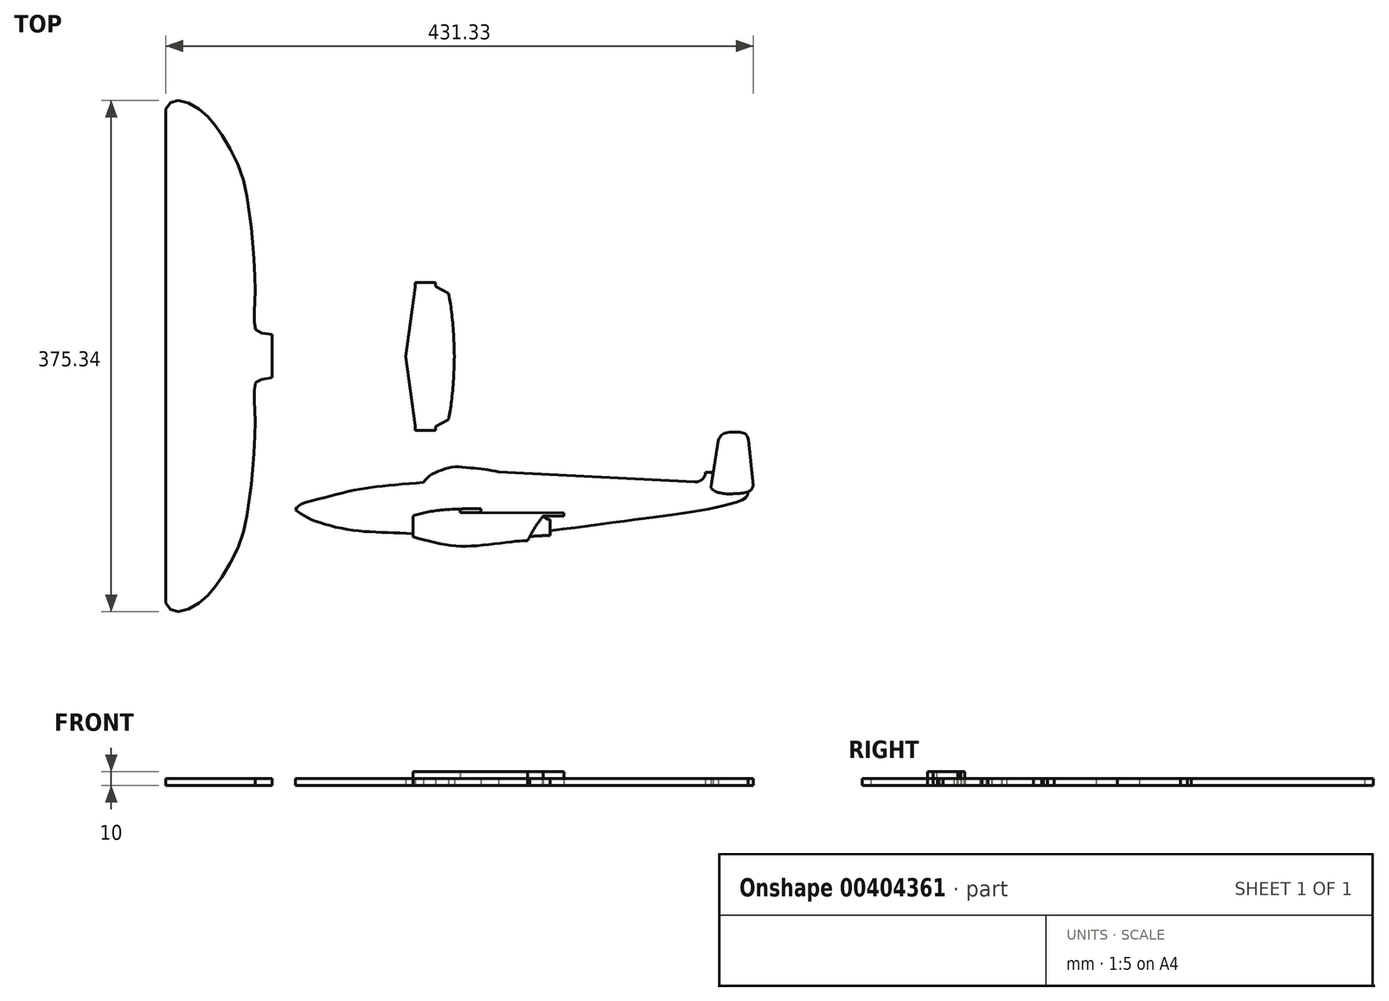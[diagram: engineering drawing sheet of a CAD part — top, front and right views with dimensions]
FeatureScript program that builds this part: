
annotation { "Feature Type Name" : "Feature", "Feature Type Description" : "" }
export const myFeature = defineFeature(function(context is Context, id is Id, definition is map)
    precondition{}
    {
        {
            var Q0;
            Q0=qCreatedBy(makeId("Top.planeOp"),FACE);
            var sketch = newSketch(context, id + "F0", { "sketchPlane" : qUnion([Q0])});
            skLineSegment(sketch, "E0", {"start": v(-207.66, -171.28) * mm, "end": v(-207.66, 10) * mm});
            skFitSpline(sketch, "E1", {"points": [v(-207.66, 10) * mm, v(-202.85, 15.7) * mm, v(-191.9, 14.82) * mm, v(-178.34, 6.06) * mm, v(-168.71, -5.75) * mm, v(-153.4, -33.76) * mm, v(-146.4, -65.7) * mm, v(-143.33, -93.72) * mm, v(-142.01, -124.35) * mm, v(-142.45, -136.6) * mm, v(-142.45, -149.3) * mm, v(-140.26, -153.23) * mm, v(-129.76, -155.42) * mm], "startDerivative": vector(68.67, 123.88) * mm, "endDerivative": vector(186.35, -20.01) * mm});
            skLineSegment(sketch, "E2", {"start": v(-129.76, -155.42) * mm, "end": v(-129.76, -171.28) * mm});
            skLineSegment(sketch, "E3.MirrorCS", {"start": v(-207.66, -171.28) * mm, "end": v(-207.66, -352.57) * mm});
            skLineSegment(sketch, "E4.MirrorCS", {"start": v(-129.76, -187.14) * mm, "end": v(-129.76, -171.28) * mm});
            skFitSpline(sketch, "E5.MirrorCS", {"points": [v(-207.66, -352.57) * mm, v(-202.85, -358.25) * mm, v(-191.9, -357.38) * mm, v(-178.34, -348.63) * mm, v(-168.71, -336.81) * mm, v(-153.4, -308.8) * mm, v(-146.4, -276.86) * mm, v(-143.33, -248.85) * mm, v(-142.01, -218.21) * mm, v(-142.45, -205.96) * mm, v(-142.45, -193.27) * mm, v(-140.26, -189.33) * mm, v(-129.76, -187.14) * mm], "startDerivative": vector(68.67, -123.88) * mm, "endDerivative": vector(186.35, 20.01) * mm});
            skFitSpline(sketch, "E6", {"points": [v(-112.4, -284.3) * mm, v(-109.82, -280.98) * mm, v(-92.52, -275.46) * mm, v(-68.6, -269.57) * mm, v(-48, -266.63) * mm, v(-18.55, -264.05) * mm], "startDerivative": vector(17.03, 35.63) * mm, "endDerivative": vector(121.12, 9.89) * mm});
            skFitSpline(sketch, "E7", {"points": [v(-18.55, -264.05) * mm, v(-13.4, -258.9) * mm, v(-4.94, -254.85) * mm, v(4.26, -252.65) * mm, v(16.4, -253.38) * mm, v(26.71, -254.49) * mm, v(36.65, -256.33) * mm], "startDerivative": vector(31.81, 38.04) * mm, "endDerivative": vector(58.7, -12.14) * mm});
            skLineSegment(sketch, "E8", {"start": v(36.65, -256.33) * mm, "end": v(180.9, -263.69) * mm});
            skArc(sketch, "E9", {"start": v(180.9, -263.69) * mm, "mid": v(186.22, -261.8) * mm, "end": v(188.63, -256.7) * mm});
            skLineSegment(sketch, "E10", {"start": v(188.63, -256.7) * mm, "end": v(215.5, -256.7) * mm});
            skFitSpline(sketch, "E11", {"points": [v(215.5, -256.7) * mm, v(219.18, -265.53) * mm, v(219.91, -271.05) * mm, v(218.44, -275.1) * mm, v(206.67, -279.88) * mm, v(183.11, -285.03) * mm, v(148.52, -289.81) * mm, v(90.38, -297.54) * mm, v(23.4, -303.06) * mm, v(-35.11, -301.22) * mm, v(-70.8, -299.01) * mm, v(-100.62, -291.29) * mm, v(-112.4, -284.3) * mm], "startDerivative": vector(85.33, -181.2) * mm, "endDerivative": vector(-165, 117.6) * mm});
            skLineSegment(sketch, "E12", {"start": v(-25.95, -288.57) * mm, "end": v(-25.95, -304.06) * mm});
            skLineSegment(sketch, "E13", {"start": v(74.67, -291.4) * mm, "end": v(74.67, -302.86) * mm});
            skFitSpline(sketch, "E14", {"points": [v(23.76, -283.27) * mm, v(0, -283.88) * mm, v(-15.1, -285.68) * mm, v(-25.95, -288.57) * mm], "startDerivative": vector(-62.09, -0.7) * mm, "endDerivative": vector(-37.97, -11.96) * mm});
            skFitSpline(sketch, "E15", {"points": [v(-25.95, -304.06) * mm, v(0, -310.09) * mm, v(25.57, -310.09) * mm, v(51.17, -307.07) * mm, v(58.1, -306.77) * mm], "startDerivative": vector(91.04, -25.6) * mm, "endDerivative": vector(39.1, 0.17) * mm});
            skFitSpline(sketch, "E16", {"points": [v(58.1, -306.77) * mm, v(63.23, -297.43) * mm, v(69.55, -288.57) * mm], "startDerivative": vector(9.7, 19.07) * mm, "endDerivative": vector(13.2, 17.09) * mm});
            skLineSegment(sketch, "E17", {"start": v(69.55, -288.57) * mm, "end": v(84.69, -288.57) * mm});
            skLineSegment(sketch, "E18", {"start": v(23.76, -286.24) * mm, "end": v(23.76, -283.27) * mm});
            skFitSpline(sketch, "E19", {"points": [v(59.71, -303.61) * mm, v(74.67, -302.86) * mm], "startDerivative": vector(15.26, 0.75) * mm, "endDerivative": vector(15.26, 0.75) * mm});
            skLineSegment(sketch, "E20", {"start": v(84.69, -288.57) * mm, "end": v(84.69, -286.35) * mm});
            skLineSegment(sketch, "E21", {"start": v(23.76, -286.24) * mm, "end": v(84.69, -286.35) * mm});
            skLineSegment(sketch, "E22", {"start": v(8.37, -283.52) * mm, "end": v(8.37, -286.28) * mm});
            skLineSegment(sketch, "E23", {"start": v(23.76, -286.24) * mm, "end": v(8.37, -286.28) * mm});
            skFitSpline(sketch, "E24", {"points": [v(59.9, -286.3) * mm, v(66.14, -288.1) * mm, v(70.51, -289.69) * mm, v(71.8, -290.67) * mm, v(74.67, -291.4) * mm], "startDerivative": vector(18.97, -5.44) * mm, "endDerivative": vector(14.81, -2.5) * mm});
            skLineSegment(sketch, "E25", {"start": v(-24.57, -117.33) * mm, "end": v(-24.57, -120.63) * mm});
            skLineSegment(sketch, "E26", {"start": v(-24.57, -120.63) * mm, "end": v(-31.45, -171.53) * mm});
            skLineSegment(sketch, "E27", {"start": v(-24.57, -117.33) * mm, "end": v(-9.72, -117.33) * mm});
            skLineSegment(sketch, "E28", {"start": v(-9.72, -117.33) * mm, "end": v(-9.72, -120.08) * mm});
            skLineSegment(sketch, "E29", {"start": v(-9.72, -120.08) * mm, "end": v(0, -125.3) * mm});
            skFitSpline(sketch, "E30", {"points": [v(0, -125.3) * mm, v(2.66, -142.92) * mm, v(4.31, -171.53) * mm], "startDerivative": vector(6.72, -37.47) * mm, "endDerivative": vector(2.09, -54.3) * mm});
            skFitSpline(sketch, "E31.MirrorCS", {"points": [v(0, -217.75) * mm, v(2.66, -200.15) * mm, v(4.31, -171.53) * mm], "startDerivative": vector(6.72, 37.47) * mm, "endDerivative": vector(2.09, 54.3) * mm});
            skLineSegment(sketch, "E32.MirrorCS", {"start": v(-24.57, -225.73) * mm, "end": v(-9.72, -225.73) * mm});
            skLineSegment(sketch, "E33.MirrorCS", {"start": v(-9.72, -225.73) * mm, "end": v(-9.72, -222.98) * mm});
            skLineSegment(sketch, "E34.MirrorCS", {"start": v(-9.72, -222.98) * mm, "end": v(0, -217.75) * mm});
            skLineSegment(sketch, "E35.MirrorCS", {"start": v(-24.57, -225.73) * mm, "end": v(-24.57, -222.43) * mm});
            skLineSegment(sketch, "E36.MirrorCS", {"start": v(-24.57, -222.43) * mm, "end": v(-31.45, -171.53) * mm});
            skFitSpline(sketch, "E37", {"points": [v(197.94, -233.24) * mm, v(199.6, -230.08) * mm, v(202.48, -228.01) * mm, v(207.57, -227.05) * mm, v(212.25, -227.05) * mm, v(215.83, -227.46) * mm, v(219, -229.53) * mm, v(220.23, -233.24) * mm], "startDerivative": vector(10.44, 25.16) * mm, "endDerivative": vector(5.19, -28.6) * mm});
            skLineSegment(sketch, "E38", {"start": v(220.23, -233.24) * mm, "end": v(223.67, -266.4) * mm});
            skLineSegment(sketch, "E39", {"start": v(197.94, -233.24) * mm, "end": v(192.58, -267.9) * mm});
            skFitSpline(sketch, "E40", {"points": [v(192.58, -267.9) * mm, v(195.33, -270.38) * mm, v(200.14, -271.9) * mm, v(205.65, -272.45) * mm, v(212.11, -272.17) * mm, v(217.9, -271.62) * mm, v(222.15, -269.42) * mm, v(223.67, -266.4) * mm], "startDerivative": vector(19.57, -21.97) * mm, "endDerivative": vector(8.87, 27.2) * mm});
            skSolve(sketch);
        }
        {
            var Q0;
            Q0=makeQuery(id+"F0.imprint","IMPRINT",FACE,{"disambiguationData":[TD([[makeQuery(id+"F0.imprint","IMPRINT",EDGE,{"derivedFrom":sQuery(id+"F0.wireOp",EDGE,"E0")}),-1.0]])]});
            extrude(context, id + "F1", {"entities" : qUnion([Q0]), "depth" : 5 * mm});
        }
        {
            var Q0;
            Q0=makeQuery(id+"F0.imprint","IMPRINT",FACE,{"disambiguationData":[TD([[makeQuery(id+"F0.imprint","IMPRINT",EDGE,{"derivedFrom":sQuery(id+"F0.wireOp",EDGE,"E6")}),-1.0]])]});
            extrude(context, id + "F2", {"entities" : qUnion([Q0]), "depth" : 5 * mm});
        }
        {
            var Q0;
            {var subQ9=sQuery(id+"F0.wireOp",EDGE,"E22");Q0=makeQuery(id+"F0.imprint","IMPRINT",FACE,{"disambiguationData":[TD([[makeQuery(id+"F0.imprint","IMPRINT",EDGE,{"derivedFrom":subQ9}),-1.0]])]});}
            var Q1;
            {var subQ1=sQuery(id+"F0.wireOp",EDGE,"E15");Q1=makeQuery(id+"F0.imprint","IMPRINT",FACE,{"disambiguationData":[TD([[makeQuery(id+"F0.imprint","IMPRINT",EDGE,{"derivedFrom":subQ1}),1.0]])]});}
            var Q2;
            {var subQ0=sQuery(id+"F0.wireOp",EDGE,"E18");Q2=makeQuery(id+"F0.imprint","IMPRINT",FACE,{"disambiguationData":[TD([[makeQuery(id+"F0.imprint","IMPRINT",EDGE,{"derivedFrom":subQ0}),1.0]])]});}
            var Q3;
            {var subQ4=sQuery(id+"F0.wireOp",EDGE,"E17");Q3=makeQuery(id+"F0.imprint","IMPRINT",FACE,{"disambiguationData":[TD([[makeQuery(id+"F0.imprint","IMPRINT",EDGE,{"derivedFrom":subQ4}),1.0]])]});}
            var Q4;
            {var subQ0=sQuery(id+"F0.wireOp",EDGE,"E13");var subQ1=sQuery(id+"F0.wireOp",EDGE,"E11");var subQ2=makeQuery(id+"F0.imprint","INTERSECT",VERTEX,{"derivedFrom":[subQ1,subQ0]});Q4=makeQuery(id+"F0.imprint","IMPRINT",FACE,{"disambiguationData":[TD([[makeQuery(id+"F0.imprint","IMPRINT",EDGE,{"disambiguationData":[TD([[subQ2,-1.0]])],"derivedFrom":subQ1}),-1.0]])]});}
            var Q5;
            {var subQ0=sQuery(id+"F0.wireOp",EDGE,"E13");var subQ1=sQuery(id+"F0.wireOp",EDGE,"E11");var subQ2=makeQuery(id+"F0.imprint","INTERSECT",VERTEX,{"derivedFrom":[subQ1,subQ0]});Q5=makeQuery(id+"F0.imprint","IMPRINT",FACE,{"disambiguationData":[TD([[makeQuery(id+"F0.imprint","IMPRINT",EDGE,{"disambiguationData":[TD([[subQ2,-1.0]])],"derivedFrom":subQ1}),1.0]])]});}
            extrude(context, id + "F3", {"entities" : qUnion([Q0, Q1, Q2, Q3, Q4, Q5]), "depth" : 5 * mm});
        }
        {
            var Q0;
            {var subQ9=sQuery(id+"F0.wireOp",EDGE,"E22");Q0=makeQuery(id+"F0.imprint","IMPRINT",FACE,{"disambiguationData":[TD([[makeQuery(id+"F0.imprint","IMPRINT",EDGE,{"derivedFrom":subQ9}),-1.0]])]});}
            var Q1;
            {var subQ1=sQuery(id+"F0.wireOp",EDGE,"E15");Q1=makeQuery(id+"F0.imprint","IMPRINT",FACE,{"disambiguationData":[TD([[makeQuery(id+"F0.imprint","IMPRINT",EDGE,{"derivedFrom":subQ1}),1.0]])]});}
            var Q2;
            {var subQ4=sQuery(id+"F0.wireOp",EDGE,"E17");Q2=makeQuery(id+"F0.imprint","IMPRINT",FACE,{"disambiguationData":[TD([[makeQuery(id+"F0.imprint","IMPRINT",EDGE,{"derivedFrom":subQ4}),1.0]])]});}
            extrude(context, id + "F4", {"entities" : qUnion([Q0, Q1, Q2]), "depth" : 5 * mm});
        }
        {
            var Q0;
            Q0=makeQuery(id+"F4.opExtrude","SWEPT_BODY",BODY,{"disambiguationData":[OSD([sQuery(id+"F0.wireOp",EDGE,"E12"),sQuery(id+"F0.wireOp",EDGE,"E14"),sQuery(id+"F0.wireOp",EDGE,"E15"),sQuery(id+"F0.wireOp",EDGE,"E16"),sQuery(id+"F0.wireOp",EDGE,"E17"),sQuery(id+"F0.wireOp",EDGE,"E20"),sQuery(id+"F0.wireOp",EDGE,"E21"),sQuery(id+"F0.wireOp",EDGE,"E22"),sQuery(id+"F0.wireOp",EDGE,"E23")])]});
            transform(context, id + "F5", {"entities" : qUnion([Q0]), "transformType" : TransformType.TRANSLATION_3D, "dx" : 0 * mm, "dy" : 0 * mm, "dz" : 5 * mm, "makeCopy" : false});
        }
        {
            var Q0;
            Q0=makeQuery(id+"F0.imprint","IMPRINT",FACE,{"disambiguationData":[TD([[makeQuery(id+"F0.imprint","IMPRINT",EDGE,{"derivedFrom":sQuery(id+"F0.wireOp",EDGE,"E25")}),1.0]])]});
            extrude(context, id + "F6", {"entities" : qUnion([Q0]), "depth" : 5 * mm});
        }
        {
            var Q0;
            {var subQ0=sQuery(id+"F0.wireOp",EDGE,"E37");Q0=makeQuery(id+"F0.imprint","IMPRINT",FACE,{"disambiguationData":[TD([[makeQuery(id+"F0.imprint","IMPRINT",EDGE,{"derivedFrom":subQ0}),-1.0]])]});}
            var Q1;
            {var subQ0=sQuery(id+"F0.wireOp",EDGE,"E11");var subQ1=sQuery(id+"F0.wireOp",EDGE,"E10");var subQ2=makeQuery(id+"F0.imprint","INTERSECT",VERTEX,{"derivedFrom":[subQ1,subQ0]});Q1=makeQuery(id+"F0.imprint","IMPRINT",FACE,{"disambiguationData":[TD([[makeQuery(id+"F0.imprint","IMPRINT",EDGE,{"disambiguationData":[TD([[subQ2,1.0]])],"derivedFrom":subQ1}),-1.0]])]});}
            extrude(context, id + "F7", {"entities" : qUnion([Q0, Q1]), "depth" : 5 * mm});
        }
    });
